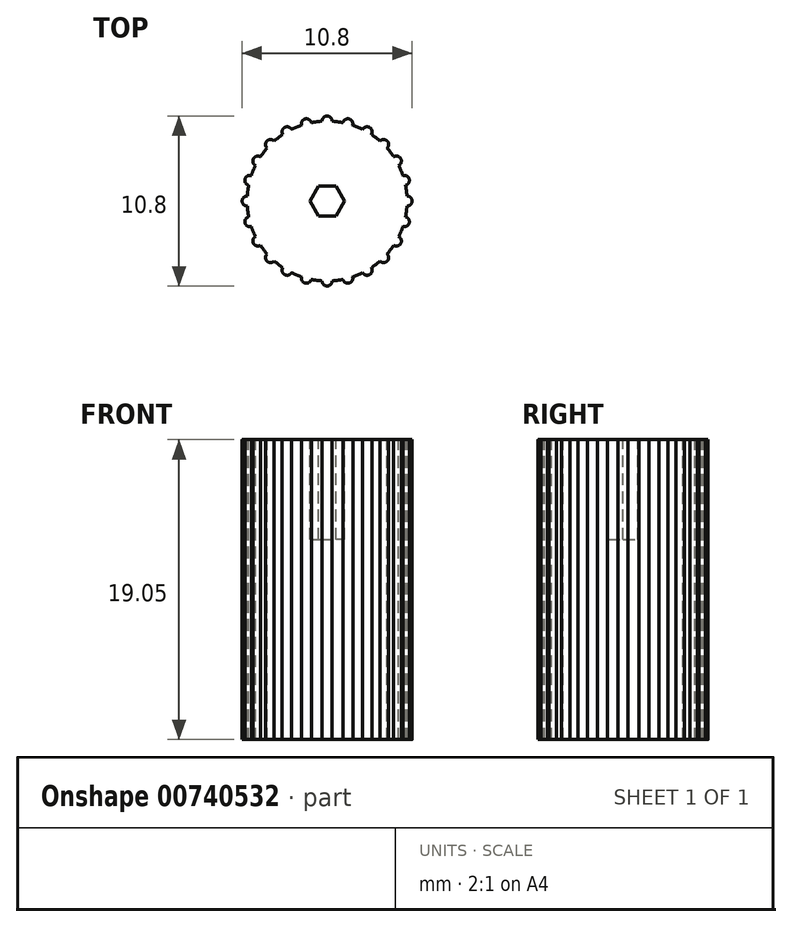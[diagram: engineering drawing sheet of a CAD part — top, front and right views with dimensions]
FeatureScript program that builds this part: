
annotation { "Feature Type Name" : "Feature", "Feature Type Description" : "" }
export const myFeature = defineFeature(function(context is Context, id is Id, definition is map)
    precondition{}
    {
        {
            var Q0;
            Q0=qCreatedBy(makeId("Top.planeOp"),FACE);
            var sketch = newSketch(context, id + "F0", { "sketchPlane" : qUnion([Q0])});
            skCircle(sketch, "E0", {"center": v(0, 0) * mm, "radius": 0.95 * mm});
            skPoint(sketch, "E1.0.midPoint", {"position": v(-1.7, 0) * mm});
            skCircle(sketch, "E2.cCircle", {"center": v(0, 0) * mm, "radius": 0.95 * mm, "construction": true});
            skLineSegment(sketch, "E2.0", {"start": v(0.55, -0.95) * mm, "end": v(-0.55, -0.95) * mm});
            skLineSegment(sketch, "E2.1", {"start": v(-0.55, -0.95) * mm, "end": v(-1.1, 0) * mm});
            skLineSegment(sketch, "E2.2", {"start": v(-1.1, 0) * mm, "end": v(-0.55, 0.95) * mm});
            skLineSegment(sketch, "E2.3", {"start": v(-0.55, 0.95) * mm, "end": v(0.55, 0.95) * mm});
            skLineSegment(sketch, "E2.4", {"start": v(0.55, 0.95) * mm, "end": v(1.1, 0) * mm});
            skLineSegment(sketch, "E2.5", {"start": v(1.1, 0) * mm, "end": v(0.55, -0.95) * mm});
            skPoint(sketch, "E2.0.midPoint", {"position": v(0, -0.95) * mm});
            skSolve(sketch);
        }
        {
            var Q0;
            Q0=qCreatedBy(makeId("Top.planeOp"),FACE);
            var sketch = newSketch(context, id + "F1", { "sketchPlane" : qUnion([Q0])});
            skCircle(sketch, "E3", {"center": v(0, 0) * mm, "radius": 5.08 * mm});
            skCircle(sketch, "E4", {"center": v(0, -5.08) * mm, "radius": 0.32 * mm});
            skCircle(sketch, "E5.1.0", {"center": v(1.31, -4.9) * mm, "radius": 0.32 * mm});
            skCircle(sketch, "E5.2.0", {"center": v(2.54, -4.4) * mm, "radius": 0.32 * mm});
            skCircle(sketch, "E5.3.0", {"center": v(3.6, -3.6) * mm, "radius": 0.32 * mm});
            skCircle(sketch, "E5.4.0", {"center": v(4.4, -2.54) * mm, "radius": 0.32 * mm});
            skCircle(sketch, "E5.5.0", {"center": v(4.9, -1.31) * mm, "radius": 0.32 * mm});
            skCircle(sketch, "E5.6.0", {"center": v(5.08, 0) * mm, "radius": 0.32 * mm});
            skCircle(sketch, "E5.7.0", {"center": v(4.9, 1.31) * mm, "radius": 0.32 * mm});
            skCircle(sketch, "E5.8.0", {"center": v(4.4, 2.54) * mm, "radius": 0.32 * mm});
            skCircle(sketch, "E5.9.0", {"center": v(3.6, 3.6) * mm, "radius": 0.32 * mm});
            skCircle(sketch, "E5.10.0", {"center": v(2.54, 4.4) * mm, "radius": 0.32 * mm});
            skCircle(sketch, "E5.11.0", {"center": v(1.31, 4.9) * mm, "radius": 0.32 * mm});
            skCircle(sketch, "E5.12.0", {"center": v(0, 5.08) * mm, "radius": 0.32 * mm});
            skCircle(sketch, "E5.13.0", {"center": v(-1.31, 4.9) * mm, "radius": 0.32 * mm});
            skCircle(sketch, "E5.14.0", {"center": v(-2.54, 4.4) * mm, "radius": 0.32 * mm});
            skCircle(sketch, "E5.15.0", {"center": v(-3.6, 3.6) * mm, "radius": 0.32 * mm});
            skCircle(sketch, "E5.16.0", {"center": v(-4.4, 2.54) * mm, "radius": 0.32 * mm});
            skCircle(sketch, "E5.17.0", {"center": v(-4.9, 1.31) * mm, "radius": 0.32 * mm});
            skCircle(sketch, "E5.18.0", {"center": v(-5.08, 0) * mm, "radius": 0.32 * mm});
            skCircle(sketch, "E5.19.0", {"center": v(-4.9, -1.31) * mm, "radius": 0.32 * mm});
            skCircle(sketch, "E5.20.0", {"center": v(-4.4, -2.54) * mm, "radius": 0.32 * mm});
            skCircle(sketch, "E5.21.0", {"center": v(-3.6, -3.6) * mm, "radius": 0.32 * mm});
            skCircle(sketch, "E5.22.0", {"center": v(-2.54, -4.4) * mm, "radius": 0.32 * mm});
            skCircle(sketch, "E5.23.0", {"center": v(-1.31, -4.9) * mm, "radius": 0.32 * mm});
            skSolve(sketch);
        }
        {
            var Q0;
            Q0 = qSketchRegion(id + "F1", true);
            extrude(context, id + "F2", {"entities" : qUnion([Q0]), "oppositeDirection" : true, "depth" : 19.05 * mm, "offsetDistance" : 25.4 * mm});
        }
        {
            var Q0;
            Q0 = qSketchRegion(id + "F0", true);
            extrude(context, id + "F3", {"entities" : qUnion([Q0]), "operationType" : NewBodyOperationType.REMOVE, "oppositeDirection" : true, "depth" : 6.35 * mm, "offsetDistance" : 25.4 * mm});
        }
    });
